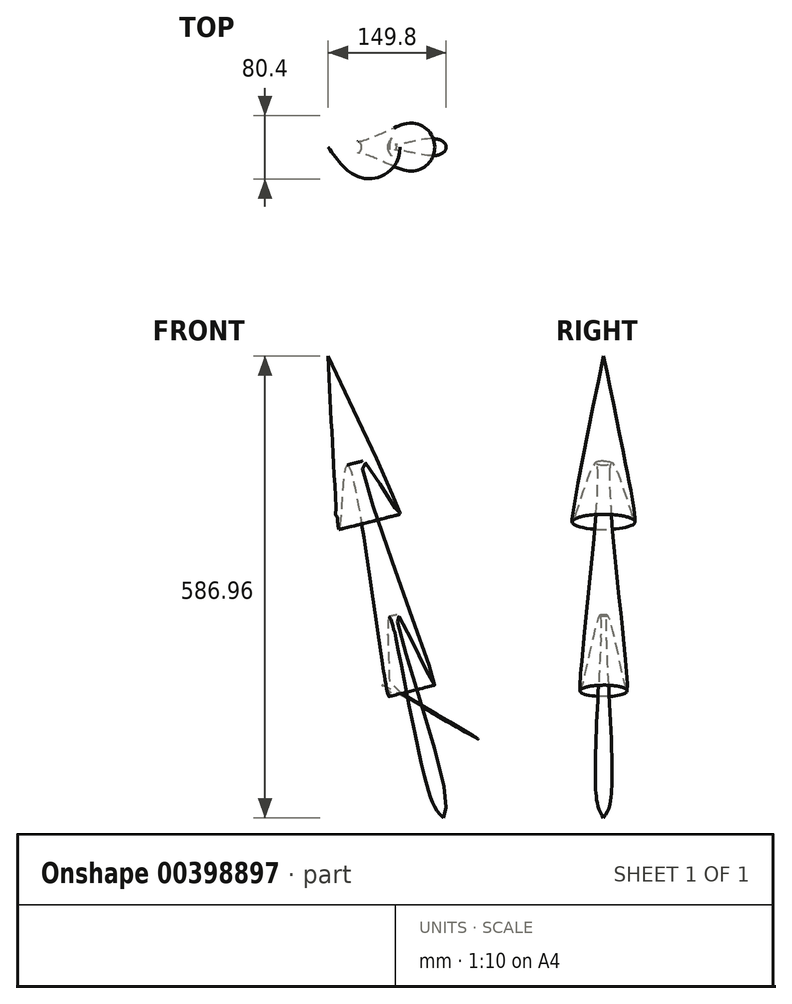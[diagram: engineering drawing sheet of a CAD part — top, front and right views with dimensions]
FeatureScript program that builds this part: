
annotation { "Feature Type Name" : "Feature", "Feature Type Description" : "" }
export const myFeature = defineFeature(function(context is Context, id is Id, definition is map)
    precondition{}
    {
        {
            var Q0;
            Q0=qCreatedBy(makeId("Front.planeOp"),FACE);
            var sketch = newSketch(context, id + "F0", { "sketchPlane" : qUnion([Q0])});
            skLineSegment(sketch, "E0", {"start": v(-53.58, 44.8) * mm, "end": v(92.97, -542.15) * mm});
            skFitSpline(sketch, "E1", {"points": [v(92.97, -542.15) * mm, v(92.97, -499.13) * mm, v(34.62, -284.43) * mm, v(81.78, -373.36) * mm, v(-10.57, -89.42) * mm, v(35.3, -153.96) * mm, v(-53.58, 44.8) * mm], "startDerivative": vector(93.27, 260.32) * mm, "endDerivative": vector(-763.35, 1613.31) * mm});
            skSolve(sketch);
        }
        {
            var Q0;
            Q0=makeQuery(id+"F0.imprint","IMPRINT",FACE,{"disambiguationData":[TD([[makeQuery(id+"F0.imprint","IMPRINT",EDGE,{"derivedFrom":sQuery(id+"F0.wireOp",EDGE,"E0")}),1.0]])]});
            var Q1;
            Q1=sQuery(id+"F0.wireOp",EDGE,"E0");
            revolve(context, id + "F1", {"entities" : qUnion([Q0]), "axis" : qUnion([Q1]), "revolveType" : RevolveType.FULL});
        }
    });
